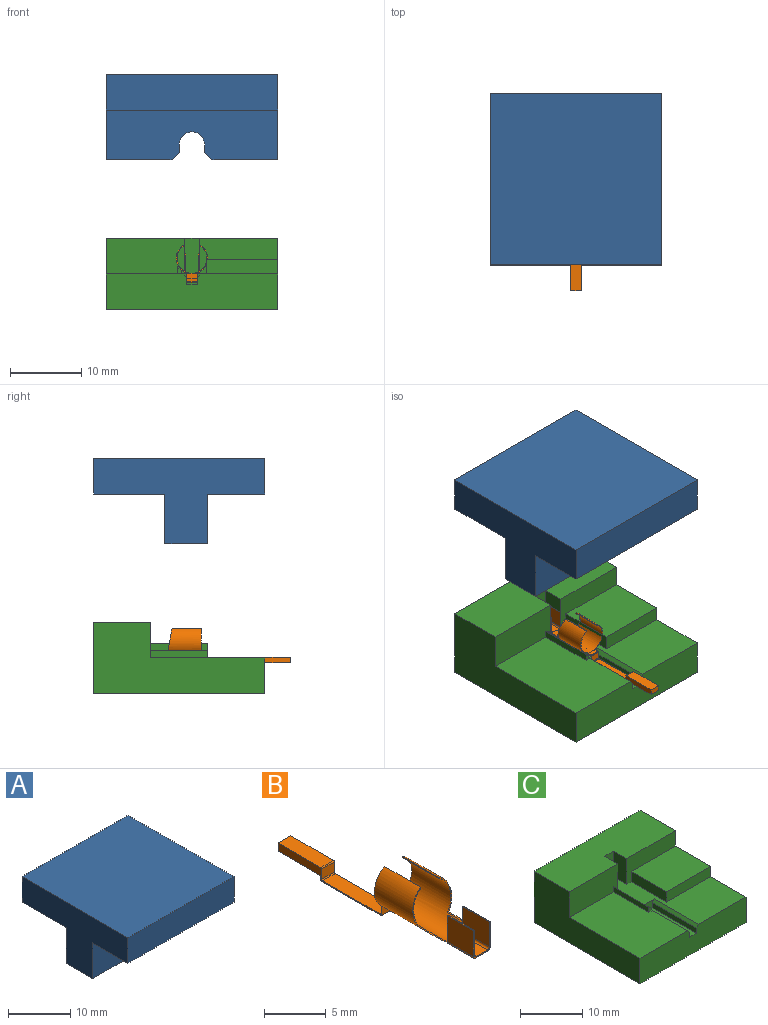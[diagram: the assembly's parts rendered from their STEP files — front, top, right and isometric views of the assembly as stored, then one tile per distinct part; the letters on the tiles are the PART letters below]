
ASSEMBLY  parts=3 mates=5
PART A: 16 faces, bbox 24x24x12 mm
  f0: plane 24x12mm, normal (1,0,0), area 162mm2, adj f2,f3,f5,f6,f7,f8,f9,f13
  f1: extruded ~6x3.6mm, area 35.4mm2, adj f7,f8,f10,f12
  f2: plane 24x5mm, normal (0,1,0), area 120mm2, adj f0,f4,f5,f9
  f3: plane 24x5mm, normal (0,-1,0), area 120mm2, adj f0,f4,f5,f6
  f4: plane 24x12mm, normal (-1,0,0), area 162mm2, adj f2,f3,f5,f6,f7,f8,f9,f11
  f5: plane 24x24mm, normal (0,0,1), area 576mm2, adj f0,f2,f3,f4
  f6: plane 24x8mm, normal (0,0,-1), area 192mm2, adj f0,f3,f4,f7
  f7: plane 24x7mm, normal (0,-1,0), area 154.3mm2, adj f0,f1,f4,f6,f10,f11,f12,f13
  f8: plane 24x7mm, normal (0,1,0), area 154.3mm2, adj f0,f1,f4,f9,f10,f11,f12,f13
  f9: plane 24x10mm, normal (0,0,-1), area 240mm2, adj f0,f2,f4,f8
  f10: plane 6x1mm, normal (1,0,0), area 6mm2, adj f1,f7,f8,f15
  f11: plane 9.2x6mm, normal (0,0,-1), area 55.2mm2, adj f4,f7,f8,f15
  f12: plane 6x1mm, normal (-1,0,0), area 6mm2, adj f1,f7,f8,f14
  f13: plane 9.2x6mm, normal (0,0,-1), area 55.2mm2, adj f0,f7,f8,f14
  f14: plane 6x1mm, normal (-0.71,0,-0.71), area 8.5mm2, adj f7,f8,f12,f13
  f15: plane 6x1mm, normal (0.71,0,-0.71), area 8.5mm2, adj f7,f8,f10,f11
PART B: 53 faces, bbox 4.4x22.6x5.4 mm
  f0: plane 0.67x0.49mm, normal (0,-1,0), area 0.1mm2, adj f3,f5,f35,f39
  f1: plane 0.85x0.18mm, normal (0,-1,0), area 0mm2, adj f3,f5,f44,f49
  f2: plane 0.85x0.18mm, normal (0,-1,0), area 0mm2, adj f3,f5,f44,f52
  f3: cylinder r=2.1mm len=7.1mm, axis (0,1,0), area 57.7mm2, adj f0,f1,f2,f4,f6,f7,f8,f9
  f4: plane 4.12x0.11mm, normal (1,0,0), area 0.5mm2, adj f3,f5,f9,f34
  f5: cylinder r=2.2mm len=7.1mm, axis (0,1,0), area 61.4mm2, adj f0,f1,f2,f4,f6,f7,f8,f9
  f6: plane 4.12x0.11mm, normal (-1,0,0), area 0.5mm2, adj f3,f5,f7,f32
  f7: plane 4.06x2.2mm, normal (0,1,0), area 0.5mm2, adj f3,f5,f6,f11
  f8: plane 0.67x0.49mm, normal (0,-1,0), area 0.1mm2, adj f3,f5,f33,f41
  f9: plane 4.06x2.2mm, normal (0,1,0), area 0.5mm2, adj f3,f4,f5,f11
  f10: plane 0.73x0.1mm, normal (0,-1,0), area 0mm2, adj f5,f11,f13,f14
  f11: plane 1.45x0.6mm, normal (0,0,1), area 0.9mm2, adj f7,f9,f10,f12,f14,f15,f25
  f12: plane 12.5x1.3mm, normal (1,0,0), area 4.9mm2, adj f11,f13,f15,f16,f17,f18,f19,f20
  f13: plane 1.45x0.5mm, normal (0,0,-1), area 0.7mm2, adj f10,f12,f14,f15,f31
  f14: plane 12.5x1.3mm, normal (-1,0,0), area 4.9mm2, adj f10,f11,f13,f16,f17,f18,f19,f20
  f15: plane 0.73x0.1mm, normal (0,-1,0), area 0mm2, adj f5,f11,f12,f13
  f16: plane 1.45x1mm, normal (0,-1,0), area 1.4mm2, adj f12,f14,f29,f31
  f17: plane 1.45x1mm, normal (0,1,0), area 1.4mm2, adj f12,f14,f25,f26
  f18: plane 6.6x1.45mm, normal (0,0,1), area 9.6mm2, adj f12,f14,f26,f27
  f19: plane 1.45x1mm, normal (0,-1,0), area 1.5mm2, adj f12,f14,f27,f28
  f20: plane 4.9x1.45mm, normal (0,0,1), area 7.1mm2, adj f12,f14,f21,f28
  f21: plane 1.45x0.8mm, normal (0,1,0), area 1.2mm2, adj f12,f14,f20,f22
  f22: plane 4.9x1.45mm, normal (0,0,-1), area 7.1mm2, adj f12,f14,f21,f23
  f23: plane 1.45x0.4mm, normal (0,1,0), area 0.6mm2, adj f12,f14,f22,f30
  f24: plane 6.8x1.45mm, normal (0,0,-1), area 9.9mm2, adj f12,f14,f29,f30
  f25: cylinder r=0.1mm len=1.45mm, axis (-1,0,0), area 0.2mm2, adj f11,f12,f14,f17
  f26: cylinder r=0.1mm len=1.45mm, axis (1,0,0), area 0.2mm2, adj f12,f14,f17,f18
  f27: cylinder r=0.1mm len=1.45mm, axis (1,0,0), area 0.2mm2, adj f12,f14,f18,f19
  f28: cylinder r=0.1mm len=1.45mm, axis (-1,0,0), area 0.2mm2, adj f12,f14,f19,f20
  f29: cylinder r=0.1mm len=1.45mm, axis (-1,0,0), area 0.2mm2, adj f12,f14,f16,f24
  f30: cylinder r=0.1mm len=1.45mm, axis (-1,0,0), area 0.2mm2, adj f12,f14,f23,f24
  f31: cylinder r=0.1mm len=1.45mm, axis (1,0,0), area 0.2mm2, adj f12,f13,f14,f16
  f32: plane 3.45x1.2mm, normal (0,-0.99,0.17), area 0.4mm2, adj f3,f5,f6,f33
  f33: plane 2.4x0.14mm, normal (0,0,1), area 0.3mm2, adj f3,f5,f8,f32
  f34: plane 3.45x1.2mm, normal (0,-0.99,0.17), area 0.4mm2, adj f3,f4,f5,f35
  f35: plane 2.4x0.14mm, normal (0,0,1), area 0.3mm2, adj f0,f3,f5,f34
  f36: plane 0.95x0.22mm, normal (0,1,0), area 0.1mm2, adj f5,f39,f40,f49,f50
  f37: plane 0.95x0.22mm, normal (0,1,0), area 0.1mm2, adj f5,f40,f41,f51,f52
  f38: plane 2.52x0.1mm, normal (0,1,0), area 0.2mm2, adj f3,f39,f45,f46,f49
  f39: plane 3x2.6mm, normal (-1,0,0), area 7.8mm2, adj f0,f36,f38,f46,f47,f50
  f40: plane 3x1.5mm, normal (0,0,-1), area 4.5mm2, adj f36,f37,f47,f50,f51
  f41: plane 3x2.6mm, normal (1,0,0), area 7.8mm2, adj f8,f37,f42,f47,f48,f51
  f42: plane 3x0.1mm, normal (0,0,1), area 0.3mm2, adj f41,f43,f47,f48
  f43: plane 3x2.5mm, normal (-1,0,0), area 7.5mm2, adj f42,f47,f48,f52
  f44: plane 3x1.3mm, normal (0,0,1), area 3.9mm2, adj f1,f2,f47,f49,f52
  f45: plane 3x2.5mm, normal (1,0,0), area 7.5mm2, adj f38,f46,f47,f49
  f46: plane 3x0.1mm, normal (0,0,1), area 0.3mm2, adj f38,f39,f45,f47
  f47: plane 2.8x1.9mm, normal (0,-1,0), area 0.7mm2, adj f39,f40,f41,f42,f43,f44,f45,f46
  f48: plane 2.52x0.1mm, normal (0,1,0), area 0.2mm2, adj f3,f41,f42,f43,f52
  f49: cylinder r=0.2mm len=3mm, axis (0,1,0), area 0.9mm2, adj f1,f36,f38,f44,f45,f47
  f50: cylinder r=0.2mm len=3mm, axis (0,-1,0), area 0.9mm2, adj f36,f39,f40,f47
  f51: cylinder r=0.2mm len=3mm, axis (0,1,0), area 0.9mm2, adj f37,f40,f41,f47
  f52: cylinder r=0.2mm len=3mm, axis (0,-1,0), area 0.9mm2, adj f2,f37,f43,f44,f47,f48
PART C: 25 faces, bbox 24x24x10 mm
  f0: plane 11x5mm, normal (0,-1,0), area 54.6mm2, adj f1,f5,f7,f9,f21,f22,f23
  f1: plane 24x19mm, normal (0,0,1), area 281mm2, adj f0,f2,f3,f4,f5,f9,f10,f11
  f2: plane 11x5mm, normal (0,-1,0), area 35mm2, adj f1,f4,f7,f10,f18,f19
  f3: plane 24x5mm, normal (0,-1,0), area 117.5mm2, adj f1,f4,f5,f6,f12,f13,f14,f16
  f4: plane 24x10mm, normal (1,0,0), area 176mm2, adj f1,f2,f3,f6,f7,f8,f18,f20
  f5: plane 24x10mm, normal (-1,0,0), area 160mm2, adj f0,f1,f3,f6,f7,f8
  f6: plane 24x24mm, normal (0,0,-1), area 576mm2, adj f3,f4,f5,f8
  f7: plane 24x8mm, normal (0,0,1), area 186mm2, adj f0,f2,f4,f5,f8,f9,f10,f11
  f8: plane 24x10mm, normal (0,1,0), area 240mm2, adj f4,f5,f6,f7
  f9: plane 5x3mm, normal (1,0,0), area 15mm2, adj f0,f1,f7,f11
  f10: plane 5x3mm, normal (-1,0,0), area 15mm2, adj f1,f2,f7,f11
  f11: plane 5x2mm, normal (0,-1,0), area 10mm2, adj f1,f7,f9,f10
  f12: plane 10x1mm, normal (-1,0,0), area 10mm2, adj f3,f14,f15,f17
  f13: plane 10x1mm, normal (1,0,0), area 10mm2, adj f3,f14,f15,f16
  f14: plane 10x1.5mm, normal (0,0,1), area 15mm2, adj f3,f12,f13,f15
  f15: plane 2.5x1.5mm, normal (0,-1,0), area 2.5mm2, adj f1,f12,f13,f14,f16,f17
  f16: plane 10x0.5mm, normal (0.71,0,0.71), area 7.1mm2, adj f1,f3,f13,f15
  f17: plane 10x0.5mm, normal (-0.71,0,0.71), area 7.1mm2, adj f1,f3,f12,f15
  f18: plane 10x8mm, normal (0,0,1), area 80mm2, adj f2,f4,f19,f20
  f19: plane 8x2mm, normal (-1,0,0), area 16mm2, adj f1,f2,f18,f20
  f20: plane 10x2mm, normal (0,-1,0), area 20mm2, adj f1,f4,f18,f19
  f21: plane 8x0.5mm, normal (1,0,0), area 4mm2, adj f0,f1,f22,f24
  f22: plane 8x0.5mm, normal (0.71,0,0.71), area 5.7mm2, adj f0,f21,f23,f24
  f23: plane 8x1mm, normal (-1,0,0), area 8mm2, adj f0,f1,f22,f24
  f24: plane 1x0.5mm, normal (0,-1,0), area 0.4mm2, adj f1,f21,f22,f23
PLACE A t=(-13.63,3.83,22.53)mm
PLACE B rot(axis=(0,0,-1),180deg) t=(-13.63,-11.27,1.75)mm
PLACE C t=(-13.63,3.83,-0.45)mm fixed
MATE parallel A.f0 <-> C.f4  axis (1,0,0) through (-1.63,-1.17,22.53)mm
MATE parallel C.f7 <-> A.f9  axis (0,0,1) through (-13.63,-0.09,4.55)mm
MATE parallel A.f2 <-> C.f8  axis (0,1,0) through (-13.63,3.83,25.03)mm
MATE parallel C.f11 <-> B.f47  axis (0,-1,0) through (-13.63,-1.17,4.55)mm
MATE parallel C.f1 <-> B.f40  axis (0,0,1) through (-12.63,-4.17,-0.45)mm
